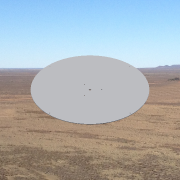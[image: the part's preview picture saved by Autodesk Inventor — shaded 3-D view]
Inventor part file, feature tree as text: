
AUTODESK INVENTOR PART (.ipt)
format: ipt  version: 2014 SP1 (Build 180222100, 222)  size: 165,888 bytes
history: native  units: in
note: dims shown in document units (in); Inventor stores cm internally (conversion verified against a paired STEP export)
features: sketch x4, extrude x2, hole x2, pattern_circular x1
ambient origin geometry x8: Origin, YZ Plane, XZ Plane, XY Plane, X Axis, Y Axis, Z Axis, Center Point
bodies: Body1 (feature_tree)
feature tree (9):
  extrude  "Extrusion1"  Depth=0.125in TaperAngle=0.0deg
  extrude  "Extrusion2"  Depth=0.125in TaperAngle=0.0deg
  hole  "Hole1"  [1 undecoded]
  pattern_circular  "Circular Pattern1"  [2 undecoded]
  hole  "Hole7"  [1 undecoded]
  sketch  "Sketch1"  dims[d0=24.0in d1=0.125in d2=0.0in]
  sketch  "Sketch2"  dims[d3=0.5in d4=0.125in d5=0.0in]
  sketch  "Sketch3"  dims[d6=11.5in]
  sketch  "Sketch9"  dims[d7=0.177in d8=0.2362in d9=0.332in d10=0.0787in d11=0.5635in d12=0.315in d13=0.8108in d14=1.5748in d15=360.0deg d85=2.2441in d86=75.0deg d87=2.2441in d88=195.0deg d89=0.2598in d90=0.2362in d91=0.4961in d92=0.0787in d93=90.0deg d94=0.315in d95=0.8108in d96=2.3622in d97=45.0deg]
note: 4 required parameter values undecoded (feature->parameter linkage not recoverable at this tier; creation-order binding heuristic only, values carry confidence <= 0.55)
